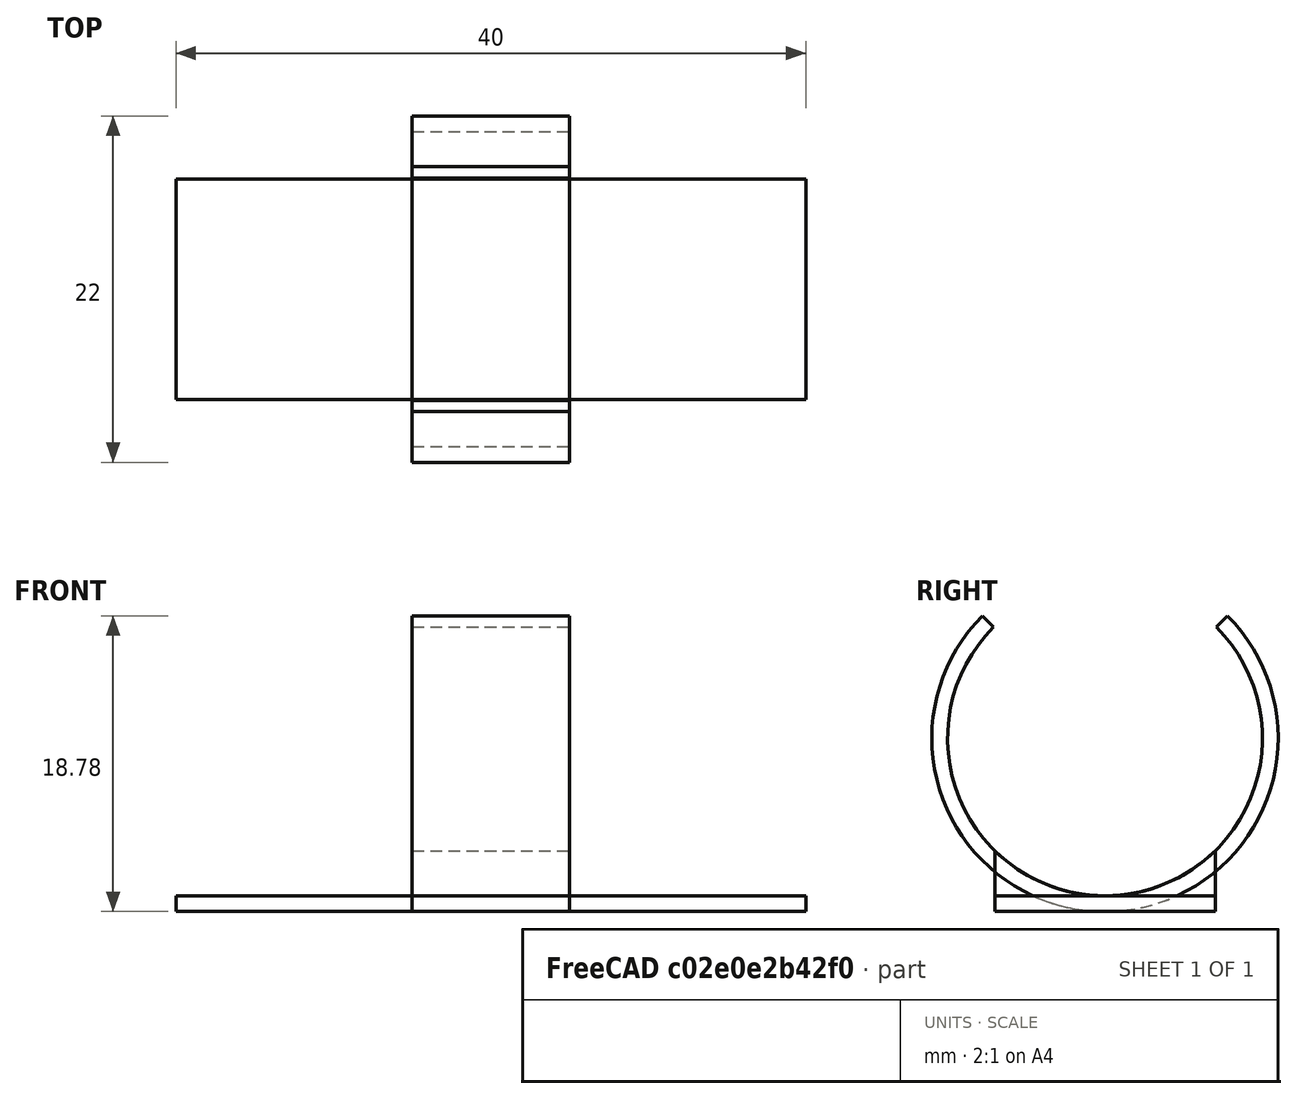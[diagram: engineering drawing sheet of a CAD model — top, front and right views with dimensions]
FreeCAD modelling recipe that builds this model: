
FCSTD DOCUMENT  (FreeCAD 0.16R)
Label: towel_labeling
License: All rights reserved
LicenseURL: http://en.wikipedia.org/wiki/All_rights_reserved
objects: Part::Box×3, Part::Cut×3, Part::Cylinder×2, Part::Chamfer×1
note: 9 computed .brp shape members not serialized (recipe doc carries the construction recipe); baked Part::Feature solids carry a one-line shape summary decoded from their .brp

FEATURE [Part::Box] Box  label="Cube"
  Height = 1
  Length = 40
  Width = 14
FEATURE [Part::Cylinder] Cylinder
  Angle = 360
  Height = 10
  Placement = pos=(15,7,11) rot=(0,1,0;1.5708rad)
  Radius = 11
FEATURE [Part::Cylinder] Cylinder001
  Angle = 360
  Height = 10
  Placement = pos=(15,7,11) rot=(0,1,0;1.5708rad)
  Radius = 10
FEATURE [Part::Box] Box001  label="Cube001"
  Height = 4
  Length = 10
  Placement = pos=(15,0,0) rot=(0,0,1;0rad)
  Width = 14
FEATURE [Part::Cut] Cut
  Base = -> Cylinder
  Tool = -> Cylinder001
FEATURE [Part::Cut] Cut001
  Base = -> Box001
  Tool = -> Cylinder001
FEATURE [Part::Box] Box002  label="Cube002"
  Height = 10
  Length = 10
  Placement = pos=(15,-3,20) rot=(0,0,1;0rad)
  Width = 20
FEATURE [Part::Chamfer] Chamfer
  Base = -> Box002
  Edges = 2 edges r=9: [Edge9,Edge11]
  Placement = pos=(0,0,-8) rot=(0,0,1;0rad)
FEATURE [Part::Cut] Cut002
  Base = -> Cut
  Tool = -> Chamfer
